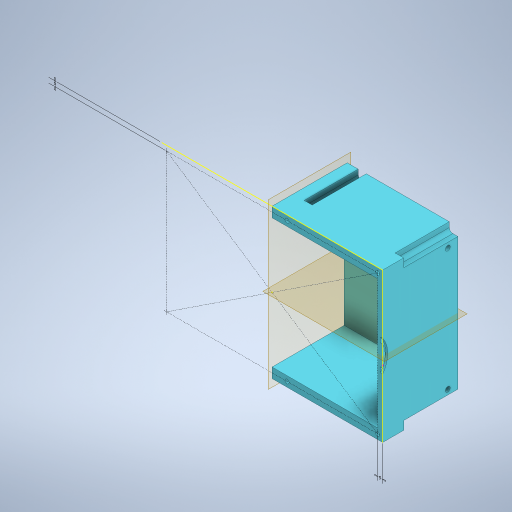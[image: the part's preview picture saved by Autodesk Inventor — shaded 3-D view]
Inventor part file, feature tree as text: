
AUTODESK INVENTOR PART (.ipt)
format: ipt  version: 2023 (Build 270158030, 158C)  size: 712,192 bytes
history: native  units: mm
features: sketch x15, extrude x14, mirror x4, hole x2, emboss x1, split x1, projected_geometry x1
ambient origin geometry x8: Origin, YZ Plane, XZ Plane, XY Plane, X Axis, Y Axis, Z Axis, Center Point
bodies: Solid1 (feature_tree)
feature tree (38):
  extrude  "MainInnerBodyExtrusion"  Depth=149.0mm
  extrude  "HoleForCamerabase"  Depth=75.0mm
  extrude  "HoleForFan"  Depth=52.0mm
  extrude  "SlotsForRearFan"  TaperAngle=0.0deg  [1 undecoded]
  sketch  "Sketch23"  dims[d8=47.0mm d9=0.0mm]
  hole  "Screw hole for 6-32 screw"  [1 undecoded]
  extrude  "Extrusion19"  Depth=3.0mm
  extrude  "Extrusion21"  Depth=60.0mm
  extrude  "Extrusion22"  Depth=4.0mm
  hole  "Hole5"  [1 undecoded]
  sketch  "Sketch31"  dims[d69=2.0mm d71=4.0mm]
  extrude  "Extrusion24"  Depth=10.0mm TaperAngle=0.0deg
  mirror  "Mirror2"
  mirror  "Mirror3"
  extrude  "Extrusion25"  Depth=15.0mm
  mirror  "Mirror4"
  mirror  "Mirror5"
  sketch  "Sketch33"  dims[d72=4.0mm d73=4.0mm]
  emboss  "Emboss1"
  extrude  "HolesForFilter"  Depth=5.0mm
  extrude  "Extrusion27"  Depth=30.0mm
  extrude  "Extrusion28"  Depth=12.0mm
  extrude  "Extrusion30"  Depth=7.0mm
  extrude  "Extrusion31"  Depth=58.0mm TaperAngle=0.0deg
  split  "Split5"
  sketch  "Sketch1"  dims[d0=220.7mm d1=149.0mm]
  sketch  "Sketch3"  dims[d2=75.0mm d3=0.0mm d5=15.7mm]
  sketch  "Sketch4"  dims[d6=52.0mm d7=57.0mm]
  sketch  "Sketch26"  dims[d13=16.0mm d14=62.0mm]
  sketch  "Sketch28"  dims[d15=3.0mm d16=47.0mm]
  sketch  "Sketch29"  dims[d17=0.0mm d67=60.0mm]
  sketch  "Sketch34"  dims[d75=4.0mm d76=10.0mm d77=0.0mm]
  sketch  "Sketch35"  dims[d79=22.0mm d95=15.0mm]
  sketch  "Sketch36"  dims[d106=5.0mm d108=5.0mm]
  sketch  "Sketch37"  dims[d116=4.051mm d117=6.0mm d118=12.7mm d119=2.362mm d120=90.0deg d121=15.0mm d122=20.594885mm d142=30.0mm]
  sketch  "Sketch39"  dims[d143=20.0mm d144=12.0mm]
  projected_geometry  "Projected Loop3"
  sketch  "Sketch40"  dims[d145=10.0mm d146=0.0mm d150=7.0mm d151=58.0mm d152=0.0mm d153=10.0mm d154=5.0mm d155=72.0mm d156=0.0mm d157=30.0mm d158=4.051mm d159=6.0mm d160=8.0mm d161=58.0mm d162=14.3117mm d163=8.0mm d164=20.594885mm d167=54.0mm d168=0.0mm d169=54.0mm d170=0.0mm d178=25.4mm d179=1.0mm d180=0.0mm d181=140.0mm d182=52.25mm d183=21.0mm d184=47.0mm d185=2.25mm d186=0.0mm d187=3.0mm d188=20.0mm d189=1.5mm d190=1.5mm d191=7.0mm d192=0.0mm d193=4.8514mm d194=5.0mm d195=10.0mm d196=10.0mm d197=5.0mm d198=9.525mm d199=0.0mm d203=40.0mm d204=2.0mm d205=0.0mm d206=2.0mm d207=0.0mm]
note: 3 required parameter values undecoded (feature->parameter linkage not recoverable at this tier; creation-order binding heuristic only, values carry confidence <= 0.55)
